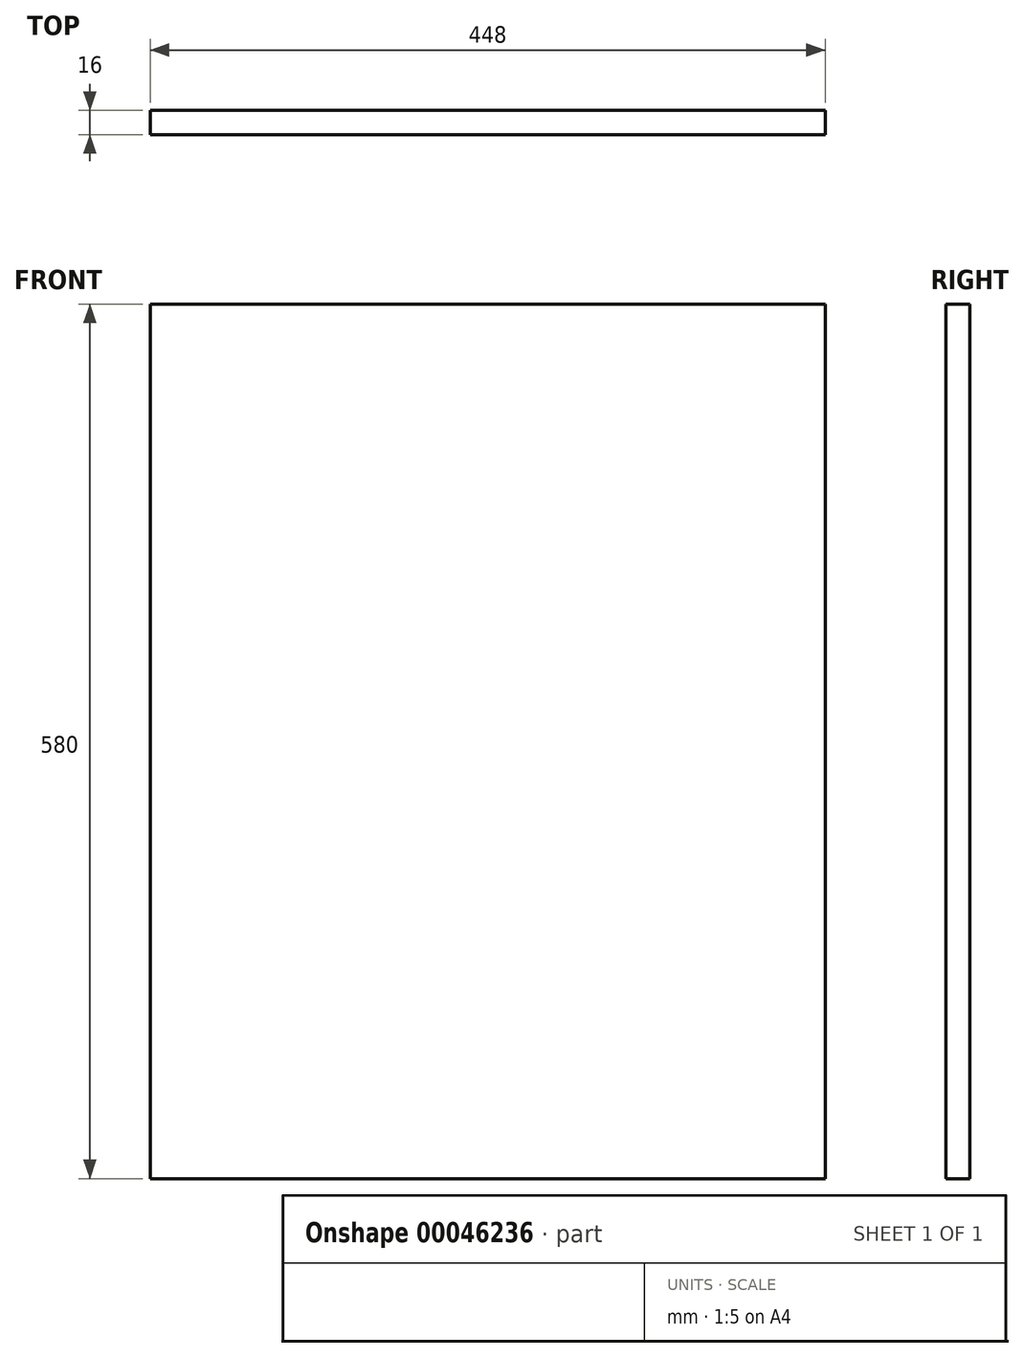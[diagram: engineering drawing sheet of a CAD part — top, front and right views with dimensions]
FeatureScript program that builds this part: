
annotation { "Feature Type Name" : "Feature", "Feature Type Description" : "" }
export const myFeature = defineFeature(function(context is Context, id is Id, definition is map)
    precondition{}
    {
        {
            var Q0;
            Q0=qCreatedBy(makeId("Front.planeOp"),FACE);
            var sketch = newSketch(context, id + "F0", { "sketchPlane" : qUnion([Q0])});
            skLineSegment(sketch, "E0.rect.bottom", {"start": v(224, 290) * mm, "end": v(-224, 290) * mm});
            skLineSegment(sketch, "E0.rect.top", {"start": v(224, -290) * mm, "end": v(-224, -290) * mm});
            skLineSegment(sketch, "E0.rect.left", {"start": v(224, 290) * mm, "end": v(224, -290) * mm});
            skLineSegment(sketch, "E0.rect.right", {"start": v(-224, 290) * mm, "end": v(-224, -290) * mm});
            skPoint(sketch, "E0.rect.middle", {"position": v(0, 0) * mm});
            skSolve(sketch);
        }
        {
            var Q0;
            Q0 = qSketchRegion(id + "F0", true);
            extrude(context, id + "F1", {"entities" : qUnion([Q0]), "depth" : 16 * mm});
        }
    });
